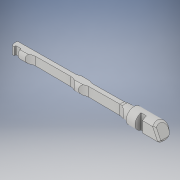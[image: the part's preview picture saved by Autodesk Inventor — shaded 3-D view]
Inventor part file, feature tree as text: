
AUTODESK INVENTOR PART (.ipt)
format: ipt  version: 2018.3 (Build 223284000, 284)  size: 279,552 bytes
history: native  units: in
note: dims shown in document units (in); Inventor stores cm internally (conversion verified against a paired STEP export)
features: sketch x3, extrude x3, revolve x1, chamfer x1, fillet x1
ambient origin geometry x8: Origin, YZ Plane, XZ Plane, XY Plane, X Axis, Y Axis, Z Axis, Center Point
bodies: Solid1 (feature_tree)
feature tree (9):
  sketch  "Sketch1"  dims[d0=0.27in d1=0.076in]
  revolve  "Revolution1"  [1 undecoded]
  extrude  "Extrusion1"  Depth=0.099in
  extrude  "Extrusion2"  Depth=0.01in
  extrude  "Extrusion3"  Depth=0.078in
  chamfer  "Chamfer1"  Distance=2.32in
  fillet  "Fillet1"  Radius=2.262in
  sketch  "Sketch2"  dims[d2=0.046in d3=0.099in]
  sketch  "Sketch3"  dims[d4=0.02in d5=0.01in d6=0.078in d7=2.32in d8=2.262in d9=0.16in d10=0.099in d11=0.14in d12=0.101in d13=0.03in d14=0.1035in d15=0.005in d16=0.01in d17=0.32in d18=0.32in d19=0.32in d20=0.32in d21=0.22in d22=0.56in d23=0.33in d24=1.53in d25=0.4in d27=90.0deg d28=1.0in d29=0.0in d30=0.28in d31=0.0in d32=0.142in d33=0.18in d34=0.28in d35=0.0in d36=0.03in d37=0.125in d38=45.0deg d39=0.125in]
note: 1 required parameter value undecoded (feature->parameter linkage not recoverable at this tier; creation-order binding heuristic only, values carry confidence <= 0.55)
